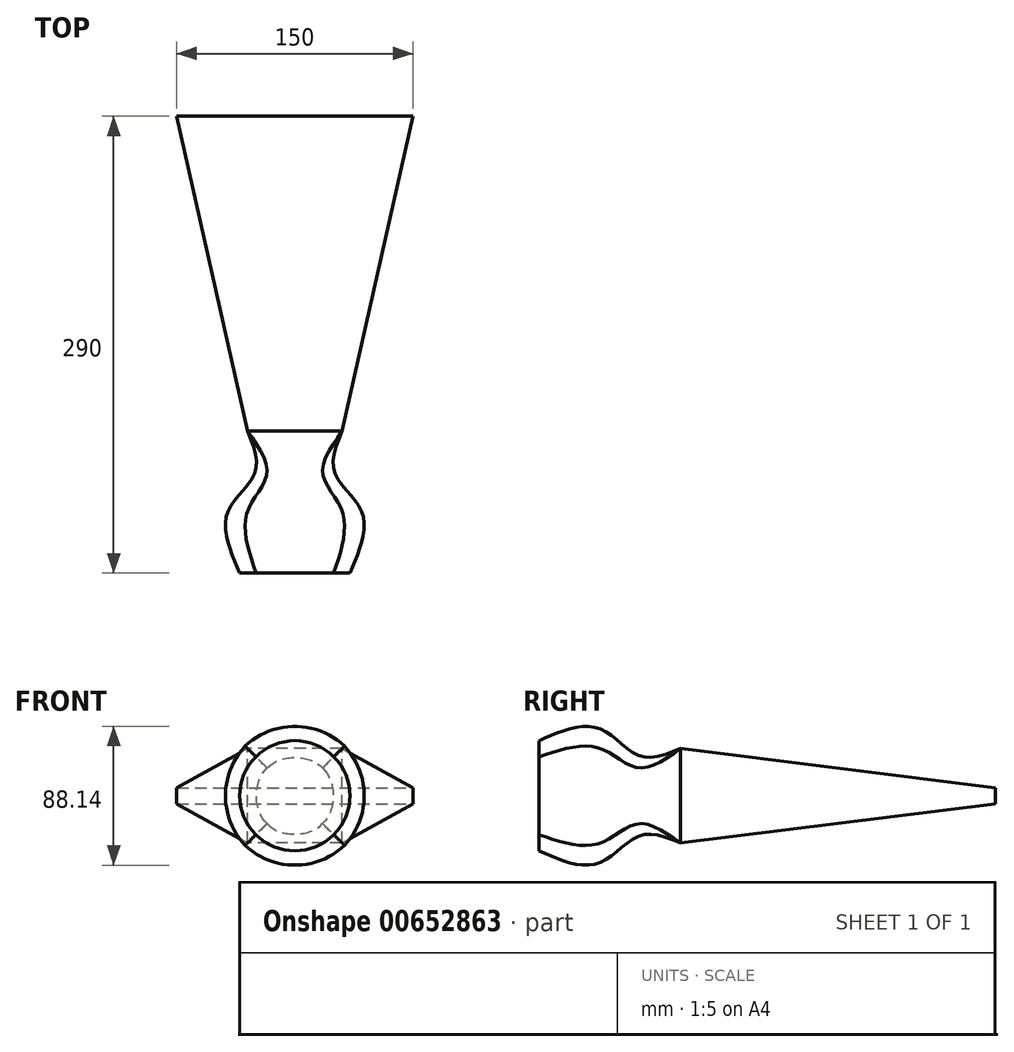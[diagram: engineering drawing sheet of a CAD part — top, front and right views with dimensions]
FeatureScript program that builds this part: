
annotation { "Feature Type Name" : "Feature", "Feature Type Description" : "" }
export const myFeature = defineFeature(function(context is Context, id is Id, definition is map)
    precondition{}
    {
        {
            var Q0;
            Q0=qCreatedBy(makeId("Front.planeOp"),FACE);
            cPlane(context, id + "F0", {"entities" : qUnion([Q0]), "cplaneType" : CPlaneType.OFFSET, "offset" : 25 * mm, "width" : 150 * mm, "height" : 150 * mm});
        }
        {
            var Q0;
            Q0=qCreatedBy(id+"F0.planeOp",FACE);
            cPlane(context, id + "F1", {"entities" : qUnion([Q0]), "cplaneType" : CPlaneType.OFFSET, "offset" : 25 * mm, "width" : 150 * mm, "height" : 150 * mm});
        }
        {
            var Q0;
            Q0=qCreatedBy(id+"F1.planeOp",FACE);
            cPlane(context, id + "F2", {"entities" : qUnion([Q0]), "cplaneType" : CPlaneType.OFFSET, "offset" : 40 * mm, "width" : 150 * mm, "height" : 150 * mm});
        }
        {
            var Q0;
            Q0=qCreatedBy(makeId("Front.planeOp"),FACE);
            var sketch = newSketch(context, id + "F3", { "sketchPlane" : qUnion([Q0])});
            skLineSegment(sketch, "E0.bottom", {"start": v(30, -30) * mm, "end": v(-30, -30) * mm});
            skLineSegment(sketch, "E0.top", {"start": v(30, 30) * mm, "end": v(-30, 30) * mm});
            skLineSegment(sketch, "E0.left", {"start": v(30, -30) * mm, "end": v(30, 30) * mm});
            skLineSegment(sketch, "E0.right", {"start": v(-30, -30) * mm, "end": v(-30, 30) * mm});
            skPoint(sketch, "E0.middle", {"position": v(0, 0) * mm});
            skSolve(sketch);
        }
        {
            var Q0;
            Q0=qCreatedBy(id+"F0.planeOp",FACE);
            var sketch = newSketch(context, id + "F4", { "sketchPlane" : qUnion([Q0])});
            skCircle(sketch, "E1", {"center": v(0, 0) * mm, "radius": 25 * mm});
            skSolve(sketch);
        }
        {
            var Q0;
            Q0=qCreatedBy(id+"F1.planeOp",FACE);
            var sketch = newSketch(context, id + "F5", { "sketchPlane" : qUnion([Q0])});
            skCircle(sketch, "E2", {"center": v(0, 0) * mm, "radius": 42 * mm});
            skSolve(sketch);
        }
        {
            var Q0;
            Q0=qCreatedBy(id+"F2.planeOp",FACE);
            var sketch = newSketch(context, id + "F6", { "sketchPlane" : qUnion([Q0])});
            skCircle(sketch, "E3", {"center": v(0, 0) * mm, "radius": 35 * mm});
            skSolve(sketch);
        }
        {
            var Q0;
            Q0 = qSketchRegion(id + "F3", true);
            var Q1;
            Q1 = qSketchRegion(id + "F4", true);
            var Q2;
            Q2 = qSketchRegion(id + "F5", true);
            var Q3;
            Q3 = qSketchRegion(id + "F6", true);
            loft(context, id + "F7", {"sheetProfilesArray" : [{ "sheetProfileEntities" : qUnion([Q0]) }, { "sheetProfileEntities" : qUnion([Q1]) }, { "sheetProfileEntities" : qUnion([Q2]) }, { "sheetProfileEntities" : qUnion([Q3]) }]});
        }
        {
            var Q0;
            Q0=qCreatedBy(makeId("Front.planeOp"),FACE);
            cPlane(context, id + "F8", {"entities" : qUnion([Q0]), "cplaneType" : CPlaneType.OFFSET, "offset" : 200 * mm, "oppositeDirection" : true, "width" : 150 * mm, "height" : 150 * mm});
        }
        {
            var Q0;
            Q0=qCreatedBy(id+"F8.planeOp",FACE);
            var sketch = newSketch(context, id + "F9", { "sketchPlane" : qUnion([Q0])});
            skLineSegment(sketch, "E4.bottom", {"start": v(-75, 5) * mm, "end": v(75, 5) * mm});
            skLineSegment(sketch, "E4.top", {"start": v(-75, -5) * mm, "end": v(75, -5) * mm});
            skLineSegment(sketch, "E4.left", {"start": v(-75, 5) * mm, "end": v(-75, -5) * mm});
            skLineSegment(sketch, "E4.right", {"start": v(75, 5) * mm, "end": v(75, -5) * mm});
            skPoint(sketch, "E4.middle", {"position": v(0, 0) * mm});
            skSolve(sketch);
        }
        {
            var Q1;
            Q1 = qSketchRegion(id + "F3", true);
            var Q2;
            Q2 = qSketchRegion(id + "F9", true);
            loft(context, id + "F10", {"operationType" : NewBodyOperationType.ADD, "sheetProfilesArray" : [{ "sheetProfileEntities" : qUnion([Q1]) }, { "sheetProfileEntities" : qUnion([Q2]) }]});
        }
    });
